# Revit family: HZ 1515 en
name_source: partatom
category: Rohrzubehör
revit_build: Autodesk Revit 2017 (Build: 20160225_1515(x64)
units: mm (PartAtom-declared; Revit-internal decimal feet)

## family parameters
Arbeitsebenenbasiert = Nein
Beim Laden mit Abzugskörper schneiden = Nein
Bemaßung runder Anschluss = Durchmesser verwenden
Gemeinsam genutzt = Nein
Immer vertikal = Ja
Teiletyp = Ventil - Zerlegung in

## types (1)
- DN
    Armaturentyp = Festwiderstand (z.B. Absperrarmatur, Schmutzfänger, Druckminderer, Kondensatregler, RL-Temperaturbegrenzer, Kappenventil)
    Armaturentyp über Funktion berechnen = nein
    BIM = https://media.live.bim.site
    BIMSITE_PRODUCT_ID = d6e4b5aef615233df98ee43589c3f629e914d9c8
    Beschreibung = Heizkörperanschluss
    CONNECTOR0_DIAMETER_dX_0r = 15 mm
    CONNECTOR0_dX_00 = 48 mm
    CONNECTOR0_dX_01 = 24 mm
    CONNECTOR0_ref_dX = 24 mm
    CONNECTOR0_ref_dZ = 105 mm
    CONNECTOR1_DIAMETER_dX_0r = 15 mm
    CONNECTOR1_dX_00 = 22 mm
    CONNECTOR1_dX_01 = 47 mm
    CONNECTOR1_ref_dX = 47 mm
    CONNECTOR1_ref_dZ = 70 mm
    CONNECTOR2_DIAMETER_dY_0r = 15 mm
    CONNECTOR2_dY_00 = 10 mm  [stored 0.0328084 ft]
    CONNECTOR3_DIAMETER_dX_0r = 15 mm
    CONNECTOR3_dX_00 = 24 mm
    CONNECTOR3_dX_01 = 48 mm
    CONNECTOR3_ref_dX = 24 mm
    CONNECTOR3_ref_dZ = 105 mm
    CONNECTOR4_DIAMETER_dY_0r = 15 mm
    CONNECTOR4_dY_00 = 10 mm  [stored 0.0328084 ft]
    CONNECTOR4_ref_dX = 70 mm
    CONNECTOR5_DIAMETER_dX_0r = 15 mm
    CONNECTOR5_dX_00 = 94 mm
    CONNECTOR5_dX_01 = 118 mm
    CONNECTOR5_ref_dX = 94 mm
    CONNECTOR5_ref_dZ = 70 mm
    DATANORM = 1515
    GTIN = 4022023303513
    HAN = 1515
    HeinzeBIM = https://www.heinze.de
    Hersteller = Hans Weitzel
    Ist System = Nein
    Ist Zubehör = Nein
    Masse (netto) [kg] = 0.6
    Maximaler Betriebsdruck (Arbeitsdruck) ps [bar] = 0.0001
    Nenndruck = 10
    Nenndrucksystem = PN
    Nennmaß = 15
    Nennweite DN = 15
    Nennweitensystem = DN
    Produktbeschreibung = HZ-Heizkörperanschluss 15mmV Press Bogen Cu/C-Stahl Pressen Springbogen Kontur V
    Produktbezeichnung = Heizkörperarmaturen für Zweirohrsysteme
    Produktklassifikation = Heizkörperanschlüsse
    Regelcharakteristik der Armatur = 1
    Typname = HZ-Heizkörperanschluss 15mmV Press Bogen Cu/C-Stahl Pressen Springbogen Kontur V
    URL = https://www.hz-weitzel.de
    VDIBSN = 002001000002000000009000000001???0000000000000000900000000
    Variante/Varianten-Art/Zubehörbezeichnung = Durchgang
    Warenhauptgruppe = Heizkörper- u. Heizungsarmaturen
    voreinstellbar/Einsatz a) = 0

note: [stored X ft] marks values corroborated as IEEE doubles in the binary element streams (Revit-internal decimal feet)
